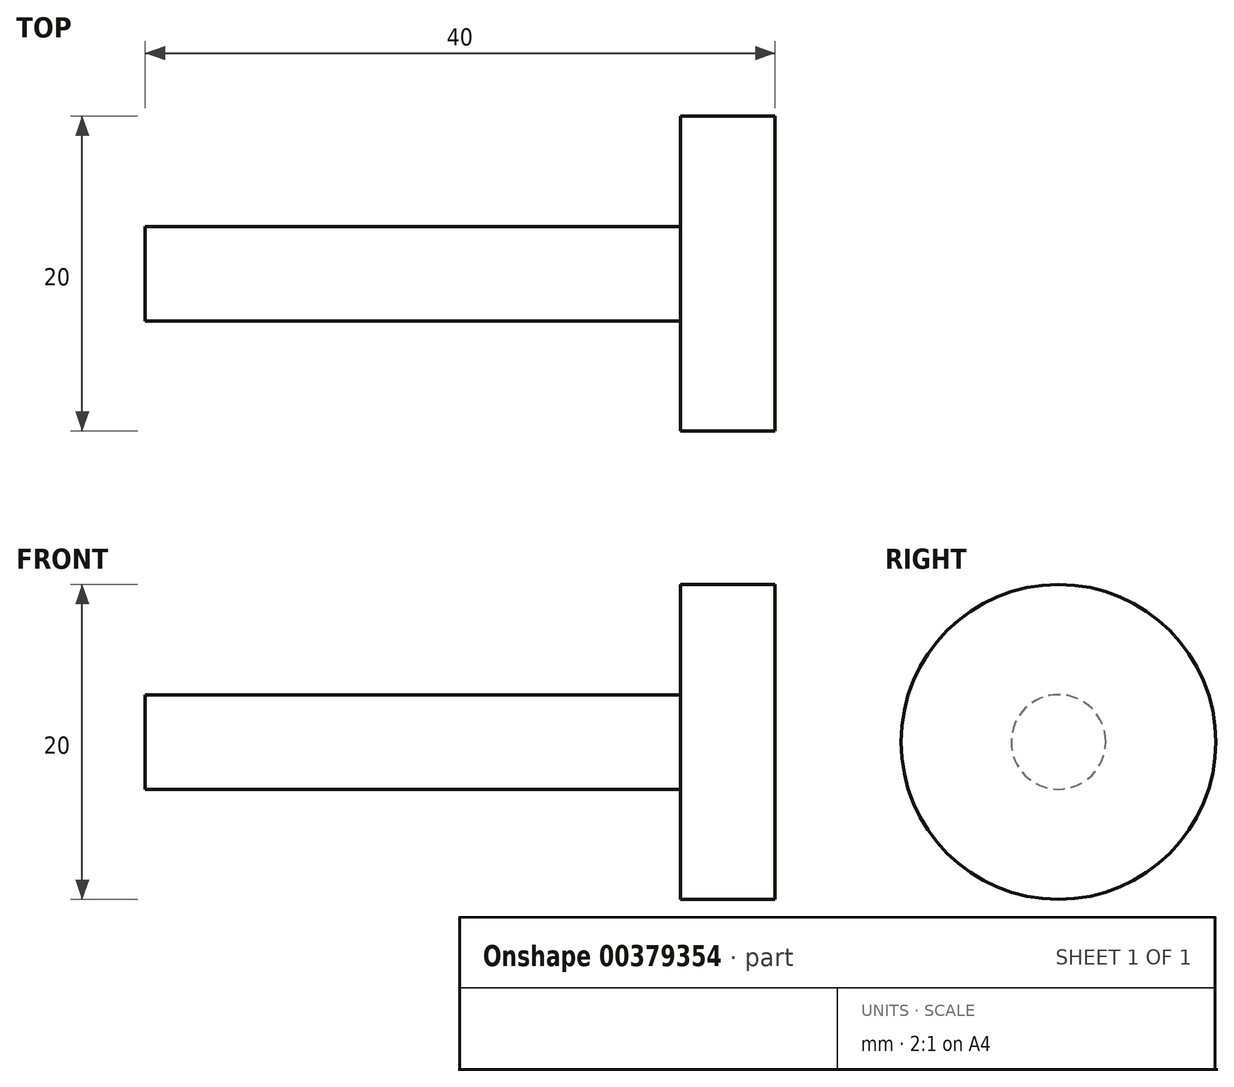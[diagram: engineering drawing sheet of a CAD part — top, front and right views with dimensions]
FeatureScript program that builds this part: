
annotation { "Feature Type Name" : "Feature", "Feature Type Description" : "" }
export const myFeature = defineFeature(function(context is Context, id is Id, definition is map)
    precondition{}
    {
        {
            var Q0;
            Q0=qCreatedBy(makeId("Front.planeOp"),FACE);
            var sketch = newSketch(context, id + "F0", { "sketchPlane" : qUnion([Q0])});
            skLineSegment(sketch, "E0", {"start": v(0, 0) * mm, "end": v(37.4, 0) * mm, "construction": true});
            skLineSegment(sketch, "E1", {"start": v(0, 0) * mm, "end": v(0, 3) * mm});
            skLineSegment(sketch, "E2", {"start": v(0, 3) * mm, "end": v(34, 3) * mm});
            skLineSegment(sketch, "E3", {"start": v(34, 3) * mm, "end": v(34, 10) * mm});
            skLineSegment(sketch, "E4", {"start": v(34, 10) * mm, "end": v(40, 10) * mm});
            skLineSegment(sketch, "E5", {"start": v(40, 10) * mm, "end": v(40, 0) * mm});
            skLineSegment(sketch, "E6", {"start": v(40, 0) * mm, "end": v(0, 0) * mm});
            skSolve(sketch);
        }
        {
            var Q0;
            Q0=makeQuery(id+"F0.imprint","IMPRINT",FACE,{"disambiguationData":[TD([[makeQuery(id+"F0.imprint","IMPRINT",EDGE,{"derivedFrom":sQuery(id+"F0.wireOp",EDGE,"E1")}),-1.0]])]});
            var Q1;
            Q1=sQuery(id+"F0.wireOp",EDGE,"E6");
            revolve(context, id + "F1", {"entities" : qUnion([Q0]), "axis" : qUnion([Q1]), "revolveType" : RevolveType.FULL});
        }
    });
